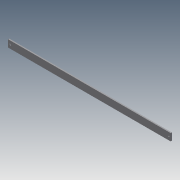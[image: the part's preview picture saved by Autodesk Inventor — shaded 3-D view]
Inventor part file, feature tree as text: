
AUTODESK INVENTOR PART (.ipt)
format: ipt  version: 2011 (Build 150239000, 239)  size: 89,088 bytes
history: native  units: in
note: dims shown in document units (in); Inventor stores cm internally (conversion verified against a paired STEP export)
features: extrude x3, sketch x3
ambient origin geometry x8: Origin, YZ Plane, XZ Plane, XY Plane, X Axis, Y Axis, Z Axis, Center Point
bodies: Solid1 (feature_tree)
feature tree (6):
  extrude  "Extrusion1"  Depth=0.5in
  extrude  "Extrusion2"  Depth=16.57in
  extrude  "Extrusion3"  Depth=0.156in
  sketch  "Sketch1"  dims[d0=17.0in d1=0.5in]
  sketch  "Sketch2"  dims[d2=8.285in d3=16.57in]
  sketch  "Sketch3"  dims[d4=0.156in d5=0.156in d6=0.125in d7=0.0in d8=0.125in d9=0.0in d10=0.125in d11=0.0in]
